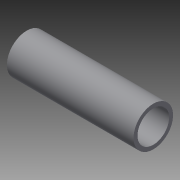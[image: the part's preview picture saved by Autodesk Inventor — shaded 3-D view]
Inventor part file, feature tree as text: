
AUTODESK INVENTOR PART (.ipt)
format: ipt  version: 2015 (Build 190159000, 159)  size: 77,312 bytes
history: native  units: in
note: dims shown in document units (in); Inventor stores cm internally (conversion verified against a paired STEP export)
features: extrude x1, sketch x1
ambient origin geometry x8: Origin, YZ Plane, XZ Plane, XY Plane, X Axis, Y Axis, Z Axis, Center Point
bodies: Solid1 (feature_tree)
feature tree (2):
  extrude  "Extrusion1"  Depth=2.0in
  sketch  "Sketch1"  dims[d0=0.5in d1=0.625in d2=2.0in d3=0.0in]
